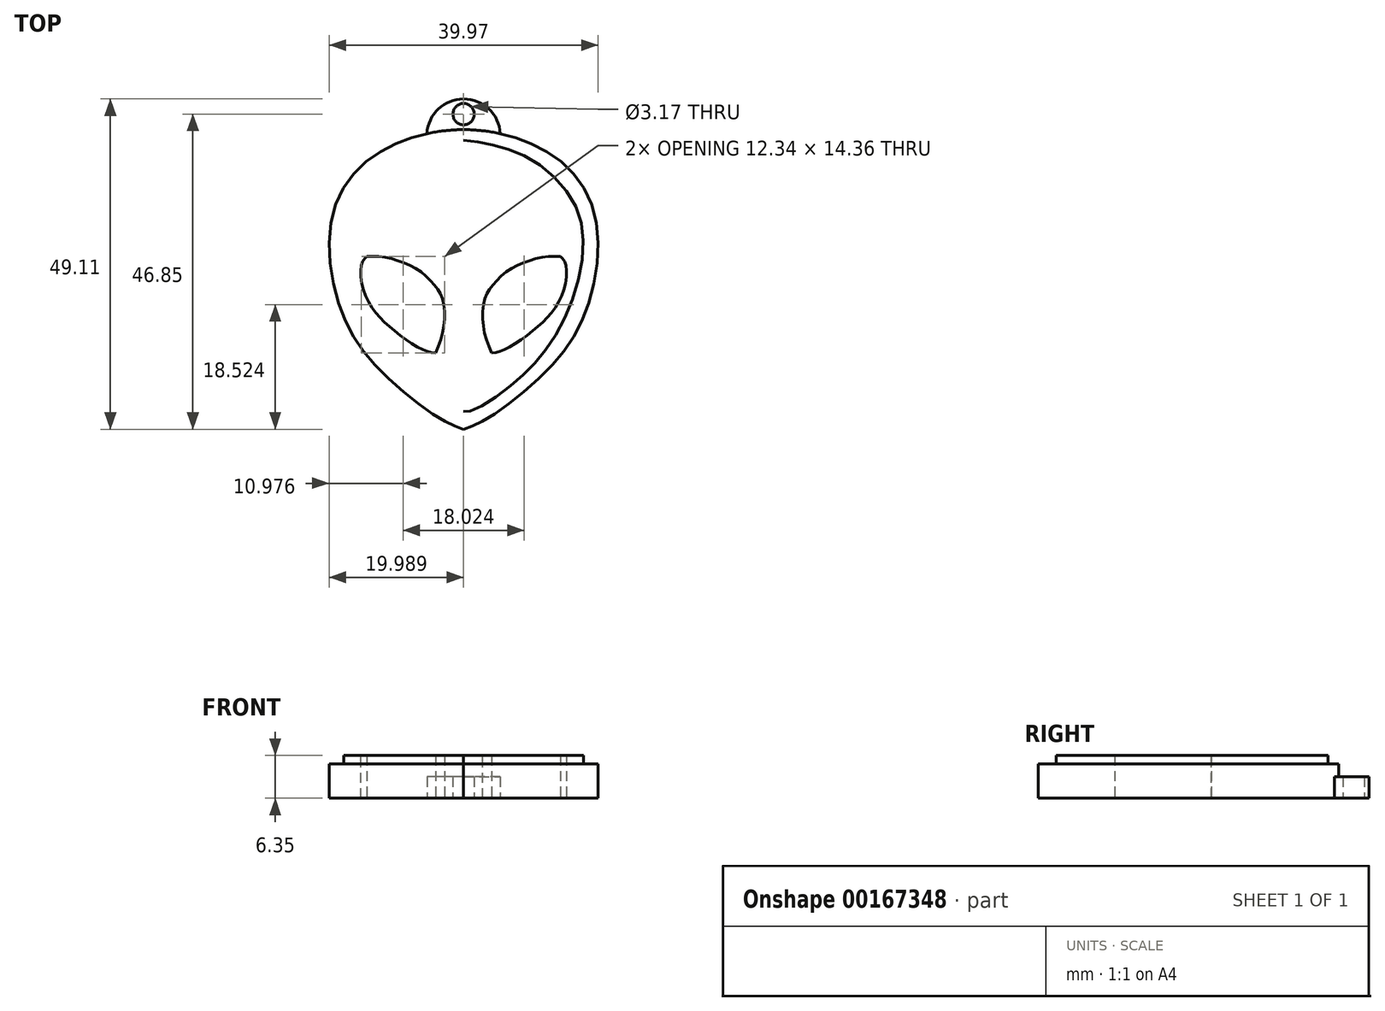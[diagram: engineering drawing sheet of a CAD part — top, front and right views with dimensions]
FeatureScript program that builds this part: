
annotation { "Feature Type Name" : "Feature", "Feature Type Description" : "" }
export const myFeature = defineFeature(function(context is Context, id is Id, definition is map)
    precondition{}
    {
        {
            var Q0;
            Q0=qCreatedBy(makeId("Top.planeOp"),FACE);
            var sketch = newSketch(context, id + "F0", { "sketchPlane" : qUnion([Q0])});
            skFitSpline(sketch, "E0", {"points": [v(-1.41, 17.89) * mm, v(-6.87, 17.26) * mm, v(-15.53, 13.38) * mm, v(-21.03, 4.63) * mm, v(-19.68, -8.9) * mm, v(-13.81, -17.93) * mm, v(-4.88, -25.14) * mm, v(-1.41, -26.7) * mm], "startDerivative": vector(-45.6, -2.32) * mm, "endDerivative": vector(32.25, -11.45) * mm});
            skFitSpline(sketch, "E1", {"points": [v(-15.8, -1) * mm, v(-13.3, -1.09) * mm, v(-10.56, -1.87) * mm, v(-8.03, -3.07) * mm, v(-6.05, -4.94) * mm, v(-4.9, -6.44) * mm, v(-4.3, -8.76) * mm, v(-4.48, -12.2) * mm, v(-5.6, -15.36) * mm], "startDerivative": vector(20.67, 0.52) * mm, "endDerivative": vector(-9.45, -22.11) * mm});
            skFitSpline(sketch, "E2", {"points": [v(-15.8, -1) * mm, v(-16.46, -1.87) * mm, v(-16.52, -5.12) * mm, v(-14.66, -9.15) * mm, v(-11.44, -12.25) * mm, v(-7.55, -14.84) * mm, v(-5.6, -15.36) * mm], "startDerivative": vector(-7.6, -6.95) * mm, "endDerivative": vector(13.59, -2) * mm});
            skFitSpline(sketch, "E3", {"points": [v(-1.41, 16.3) * mm, v(-6.42, 15.42) * mm, v(-12.84, 12.51) * mm, v(-17.98, 6.57) * mm, v(-19.13, -0.66) * mm, v(-16.56, -9.92) * mm, v(-12.37, -16.4) * mm, v(-7.5, -20.94) * mm, v(-2.57, -23.98) * mm, v(-1.41, -24.05) * mm], "startDerivative": vector(-48.17, -6.13) * mm, "endDerivative": vector(20.25, 2.77) * mm});
            skFitSpline(sketch, "E4.MirrorCS", {"points": [v(-1.41, 16.3) * mm, v(3.6, 15.42) * mm, v(10.02, 12.51) * mm, v(15.15, 6.57) * mm, v(16.3, -0.66) * mm, v(13.73, -9.92) * mm, v(9.54, -16.4) * mm, v(4.68, -20.94) * mm, v(-0.25, -23.98) * mm, v(-1.41, -24.05) * mm], "startDerivative": vector(48.17, -6.13) * mm, "endDerivative": vector(-20.25, 2.77) * mm});
            skFitSpline(sketch, "E5.MirrorCS", {"points": [v(-1.41, 17.89) * mm, v(4.04, 17.26) * mm, v(12.7, 13.38) * mm, v(18.2, 4.63) * mm, v(16.85, -8.9) * mm, v(10.99, -17.93) * mm, v(2.06, -25.14) * mm, v(-1.41, -26.7) * mm], "startDerivative": vector(45.6, -2.32) * mm, "endDerivative": vector(-32.25, -11.45) * mm});
            skFitSpline(sketch, "E6.MirrorCS", {"points": [v(12.98, -1) * mm, v(10.48, -1.09) * mm, v(7.74, -1.87) * mm, v(5.21, -3.07) * mm, v(3.22, -4.94) * mm, v(2.08, -6.44) * mm, v(1.48, -8.76) * mm, v(1.66, -12.2) * mm, v(2.77, -15.36) * mm], "startDerivative": vector(-20.67, 0.52) * mm, "endDerivative": vector(9.45, -22.11) * mm});
            skFitSpline(sketch, "E7.MirrorCS", {"points": [v(12.98, -1) * mm, v(13.64, -1.87) * mm, v(13.7, -5.12) * mm, v(11.83, -9.15) * mm, v(8.61, -12.25) * mm, v(4.73, -14.84) * mm, v(2.77, -15.36) * mm], "startDerivative": vector(7.6, -6.95) * mm, "endDerivative": vector(-13.59, -2) * mm});
            skCircle(sketch, "E8", {"center": v(-1.41, 20.15) * mm, "radius": 1.59 * mm});
            skArc(sketch, "E9", {"start": v(4.04, 17.26) * mm, "mid": v(-1.41, 22.41) * mm, "end": v(-6.87, 17.26) * mm});
            skSolve(sketch);
        }
        {
            var Q0;
            Q0=makeQuery(id+"F0.imprint","IMPRINT",FACE,{"disambiguationData":[TD([[makeQuery(id+"F0.imprint","IMPRINT",EDGE,{"derivedFrom":sQuery(id+"F0.wireOp",EDGE,"E1")}),1.0]])]});
            extrude(context, id + "F1", {"entities" : qUnion([Q0]), "depth" : 6.35 * mm});
        }
        {
            var Q0;
            Q0=makeQuery(id+"F0.imprint","IMPRINT",FACE,{"disambiguationData":[TD([[makeQuery(id+"F0.imprint","IMPRINT",EDGE,{"derivedFrom":sQuery(id+"F0.wireOp",EDGE,"E3")}),-1.0]])]});
            extrude(context, id + "F2", {"entities" : qUnion([Q0]), "operationType" : NewBodyOperationType.ADD, "depth" : 5.08 * mm});
        }
        {
            var Q0;
            Q0=makeQuery(id+"F0.imprint","IMPRINT",FACE,{"disambiguationData":[TD([[makeQuery(id+"F0.imprint","IMPRINT",EDGE,{"derivedFrom":sQuery(id+"F0.wireOp",EDGE,"E8")}),-1.0]])]});
            extrude(context, id + "F3", {"entities" : qUnion([Q0]), "operationType" : NewBodyOperationType.ADD, "depth" : 3.17 * mm});
        }
    });
